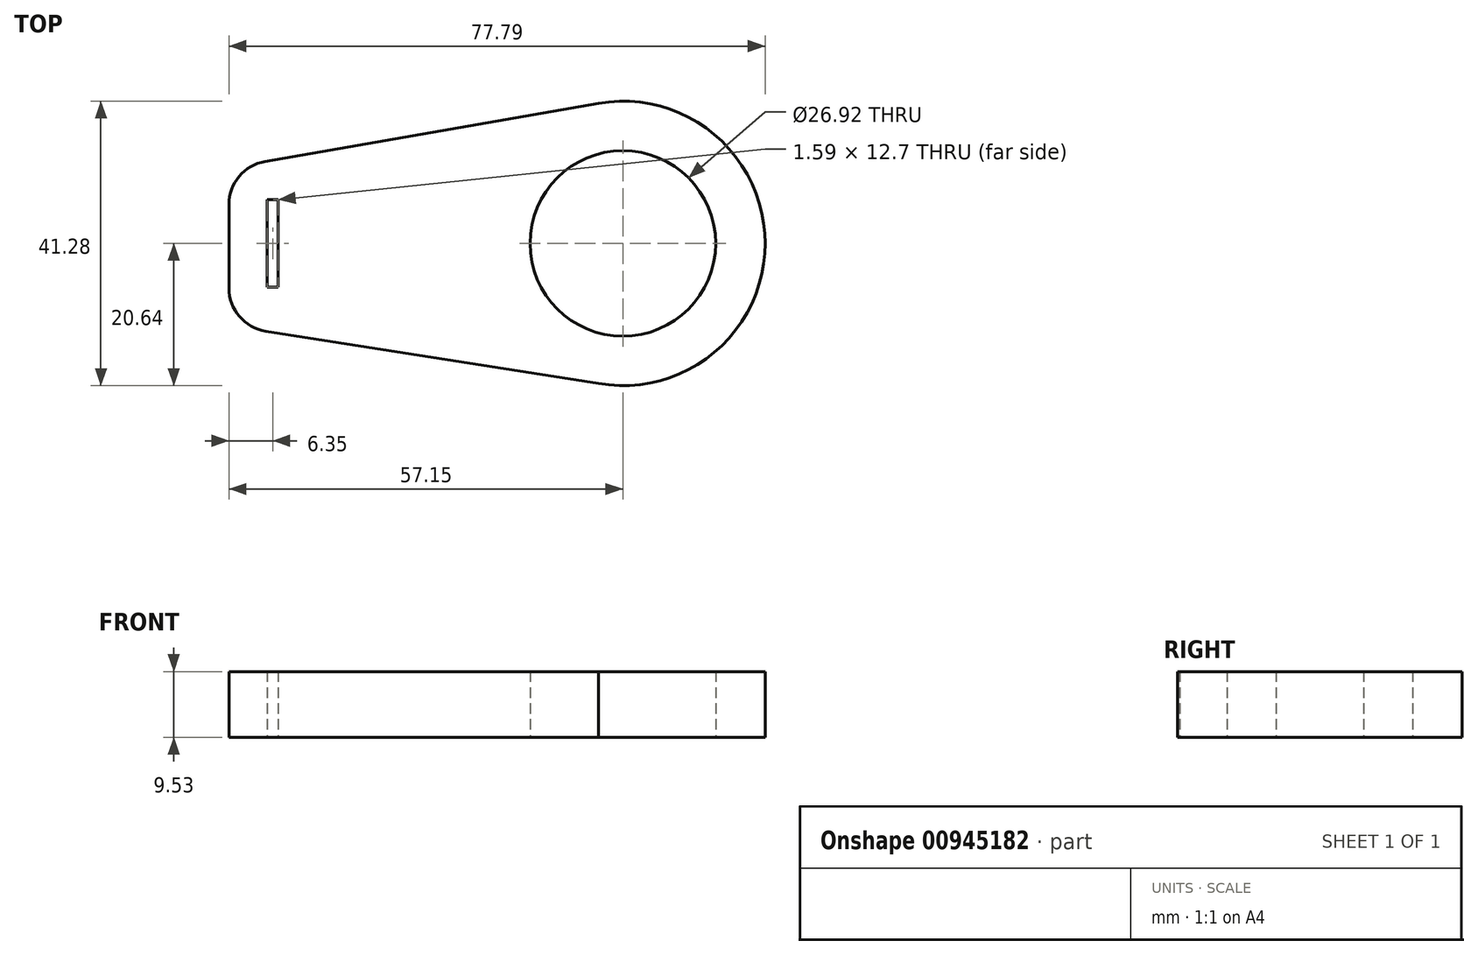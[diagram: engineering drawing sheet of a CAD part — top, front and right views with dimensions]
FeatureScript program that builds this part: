
annotation { "Feature Type Name" : "Feature", "Feature Type Description" : "" }
export const myFeature = defineFeature(function(context is Context, id is Id, definition is map)
    precondition{}
    {
        {
            var Q0;
            Q0=qCreatedBy(makeId("Top.planeOp"),FACE);
            var sketch = newSketch(context, id + "F0", { "sketchPlane" : qUnion([Q0])});
            skPoint(sketch, "E0.visualSharp", {"position": v(-45.51, 46.8) * mm});
            skCircle(sketch, "E1", {"center": v(0, 0) * mm, "radius": 13.46 * mm});
            skArc(sketch, "E2", {"start": v(-3.54, -20.33) * mm, "mid": v(20.64, 0) * mm, "end": v(-3.54, 20.33) * mm});
            skLineSegment(sketch, "E3.0", {"start": v(-50, 0) * mm, "end": v(-50, 6.35) * mm});
            skLineSegment(sketch, "E4.0", {"start": v(-51.6, 0) * mm, "end": v(-51.6, -6.35) * mm});
            skLineSegment(sketch, "E5.0", {"start": v(-50, 0) * mm, "end": v(-50, -6.35) * mm});
            skLineSegment(sketch, "E6.0", {"start": v(-51.6, 0) * mm, "end": v(-51.6, 6.35) * mm});
            skLineSegment(sketch, "E7", {"start": v(-51.6, 6.35) * mm, "end": v(-50, 6.35) * mm});
            skLineSegment(sketch, "E8", {"start": v(-51.6, -6.35) * mm, "end": v(-50, -6.35) * mm});
            skLineSegment(sketch, "E9", {"start": v(-51.9, 11.9) * mm, "end": v(-3.54, 20.33) * mm});
            skLineSegment(sketch, "E10", {"start": v(-3.54, -20.33) * mm, "end": v(-51.79, -12.74) * mm});
            skLineSegment(sketch, "E11", {"start": v(-57.15, 5.65) * mm, "end": v(-57.15, -6.46) * mm});
            skPoint(sketch, "E12.start.orphan", {"position": v(0, 20.64) * mm});
            skPoint(sketch, "E13.start.orphan", {"position": v(0, -20.64) * mm});
            skLineSegment(sketch, "E14.trimOffspring", {"start": v(-50, 0) * mm, "end": v(-50.8, 0) * mm});
            skPoint(sketch, "E15.visualSharp", {"position": v(-57.15, 10.99) * mm});
            skArc(sketch, "E15.filletArc", {"start": v(-51.9, 11.9) * mm, "mid": v(-55.66, 9.74) * mm, "end": v(-57.15, 5.65) * mm});
            skPoint(sketch, "E16.visualSharp", {"position": v(-57.15, -11.9) * mm});
            skArc(sketch, "E16.filletArc", {"start": v(-57.15, -6.46) * mm, "mid": v(-55.63, -10.59) * mm, "end": v(-51.79, -12.74) * mm});
            skSolve(sketch);
        }
        {
            var Q0;
            Q0=makeQuery(id+"F0.imprint","IMPRINT",FACE,{"disambiguationData":[TD([[makeQuery(id+"F0.imprint","IMPRINT",EDGE,{"derivedFrom":sQuery(id+"F0.wireOp",EDGE,"E1")}),-1.0]])]});
            extrude(context, id + "F1", {"entities" : qUnion([Q0]), "depth" : 9.52 * mm, "offsetDistance" : 25.4 * mm});
        }
    });
